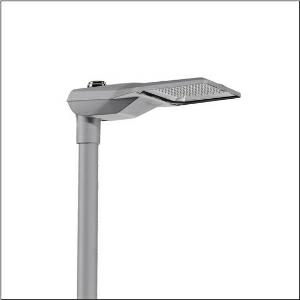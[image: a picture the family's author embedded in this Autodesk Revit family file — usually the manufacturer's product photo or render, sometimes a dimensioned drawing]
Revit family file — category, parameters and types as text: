
# Revit family: streetlight_sl_21_midi___st1_0a_5xe7d37n08lb_8a93
name_source: partatom
category: Lighting Fixtures
units: mm (PartAtom-declared; Revit-internal decimal feet)

## family parameters
Cut with Voids When Loaded = No
Host = Face
Light Source = No
Part Type = Normal
Room Calculation Point = No
Round Connector Dimension = Use Diameter
Shared = No

## types (1)
- --- (1 x LED, 14340 lm, 98.3 W, 3000K)
    Apparent Load = 98 VA
    CIE Flux Codes = 37 72 97 100 100
    Color Rendering = 70
    Color Temperature = 3000K
    Default Elevation = 1800 mm
    Description = Streetlight SL 21 midi, mast luminaire, primary light control with lens, of PMMA, primary optical cover: cover, of toughened safety glass, transparent, light distribution: ST1.0a, light emission: direct distribution, primary light characteristic: asymmetric, installation type: side-entry, LED, 3G 2.5mm², High Power LED, rated luminous flux: 14.340lm, luminous efficacy: 146lm/W, light colour: 730, colour temperature: 3000K, control gear: NEMA (7pin), control: overheat protection, pre-setting: linear dimming characteristic, constant luminous flux control, time-dependent luminous flux control, flexible luminous flux parameterisation, mains connection: 220..240V, AC, 50/60Hz, connection cable pre-assembled, cable length: 10,5m, wiring characteristics: H05VV-F, start of lifetime: 98W, end of service life: 101W, reduction: 45W, luminaire housing, of diecast aluminium (EN AC-44300), powder-coated, Siteco® metallic grey (DB 702S), corrosivity category C5 mid according to DIN EN ISO 12944, multi-level sealing system, sealing non-destructively replaceable, inclination adjustable: 0°, 5°, 10°, 15°, length: 644mm, width: 335mm, height: 110mm, spigot size: 42mm (side-entry), mounting height: 4..8m, protection rating (complete): IP66, insulation class (complete): insulation class I (protective earthing), certification: CE, ENEC, ENEC+, VDE, impact resistance: IK10, permissible operating ambient temperature for outdoor applications: -40..+50°C, standard-compliant lighting for roads and squares, packaging unit: 1 piece

Light Distribution: ST1.0a
    Height = 111 mm
    Lamp = 1 x LED
    Lamp Light Flux = 14340 lm
    Lamp Power = 98.3 W
    Lamp count = 1
    Length = 644 mm
    Luminous efficacy = 146 lm/W
    Manufacturer = Siteco
    ModVariant = No
    Model = 5XE7D37N08LB
    Number of Poles = 1
    OnlyDefault = Yes
    Power Factor = 1
    Product Name = Streetlight SL 21 midi | ST1.0a
    Product group = mast luminaire | pylon top
    ProductGroupID = 6100
    Protection Class = Protection class I
    Protection Degree = IP 66
    RLX_Detail_Level = 1
    RLX_Emergency_Light_Flux = 0 lm
    RLX_Emergency_Type = 0
    RLX_Emergency_Type_DB = No
    RlxData = <blob elided: 26717 chars, md5=79dfe1ac>
    Socket = socket
    Standby Power = 0 W
    System Light Flux = 14340 lm
    System Power = 98 W
    Type Comments = factory setting: luminous flux: 100 % | dim-lin: 254 | 1020 mA
    Type Image = l_1294377.jpg
    URL = http://relux.com
    VarID = @adj_157565
    Voltage = 0 V
    Weight = 0.00 kg
    Width = 336 mm

## geometry (parser evidence)
native form markers: Blend x4, Sweep x10
no freeform markers — native parametric forms only
